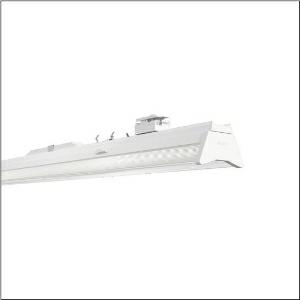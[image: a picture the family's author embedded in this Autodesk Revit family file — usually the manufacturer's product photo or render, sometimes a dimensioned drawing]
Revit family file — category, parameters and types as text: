
# Revit family: licross_r__21_performance_mo_52td167n46xg_c3aa
name_source: partatom
category: Lighting Fixtures
units: mm (PartAtom-declared; Revit-internal decimal feet)

## family parameters
Cut with Voids When Loaded = No
Host = Face
Light Source = No
Part Type = Normal
Room Calculation Point = No
Round Connector Dimension = Use Diameter
Shared = No

## types (1)
- Licross® 21 Performance MO (1 x LED, 6000 lm, 32.4 W, 4000K)
    Apparent Load = 32 VA
    CIE Flux Codes = 66 88 96 79 100
    Color Rendering = 80
    Color Temperature = 4000K
    Default Elevation = 1800 mm
    Description = Licross® 21 Performance MO, luminaire insert, of sheet steel, galvanised, coil coated, white, length: 1.500mm, width: 120mm, height: 123mm, LED rated luminous flux: 6.000lm, light colour: 840, control gear: ON/OFF, with plug, 3-pole, with phase selection, mains connection: 220..240V, AC, 50/60Hz, rated input power: 32W, internal wiring halogen-free, primary light control with lens, of plastic, primary optical cover: cover, of PMMA, light emission: direct/indirect distribution, primary light characteristic: symmetric, protection rating (complete): IP54, insulation class (complete): insulation class I (protective earthing), certification: CE, ENEC, UKCA, protection symbol: D if used in an environment with non-conductive dust loads with corresponding accessories, impact resistance: IK06, permissible ambient temperature for indoor applications: -35..+50°C, corresponds to IFS (International Featured Standards) requirements for safety and quality in the food industry, reducing of maximum allowable ambient temperature of 5°C with ceiling mounting, LABS conformity tested according to VDMA 24364:2018-05, packaging unit: 1 piece
    Height = 114 mm
    Lamp = 1 x LED
    Lamp Light Flux = 6000 lm
    Lamp Power = 32.4 W
    Lamp count = 1
    Length = 1500 mm
    Luminous efficacy = 185 lm/W
    Manufacturer = Siteco
    ModVariant = No
    Model = 52TD167N46XG
    Mounting Place = Ceiling
    Mounting Type = Pendant
    Number of Poles = 1
    OnlyDefault = Yes
    Power Factor = 1
    Product Name = Licross® 21 Performance MO
    Product group = luminaire insert | ceiling pendant
    ProductGroupID = 902
    Protection Class = Protection class I
    Protection Degree = IP 54
    RLX_Detail_Level = 1
    RLX_Emergency_Light_Flux = 0 lm
    RLX_Emergency_Type = 0
    RLX_Emergency_Type_DB = No
    RlxData = <blob elided: 30449 chars, md5=56a5f327>
    Socket = socket
    Standby Power = 0 W
    System Light Flux = 6000 lm
    System Power = 32 W
    Type Comments = Product without accessories
    Type Image = l_1256138.jpg
    URL = http://relux.com
    VarID = ---
    Voltage = 0 V
    Weight = 0.00 kg
    Width = 120 mm

## geometry (parser evidence)
native form markers: Blend x4, Sweep x12
no freeform markers — native parametric forms only
